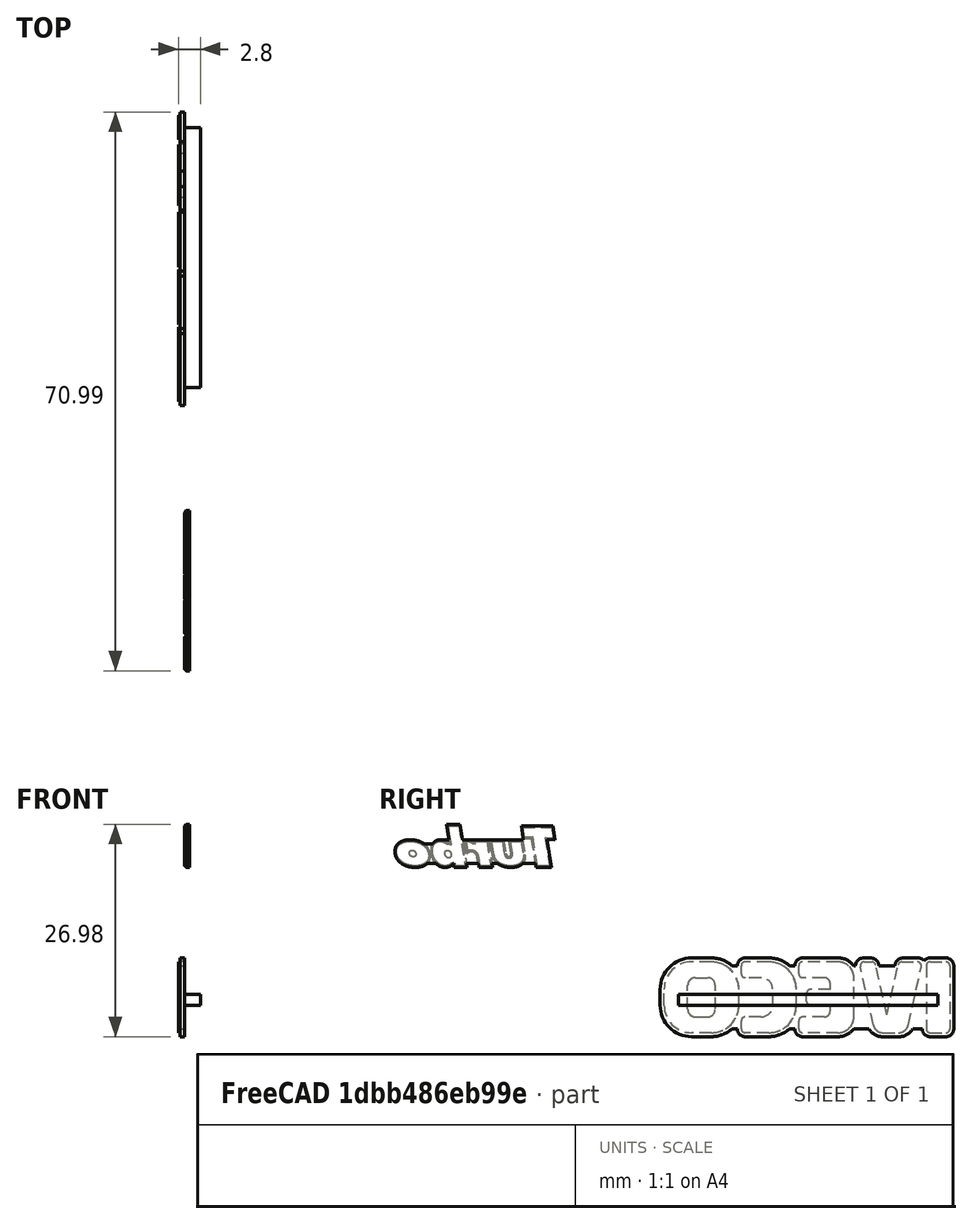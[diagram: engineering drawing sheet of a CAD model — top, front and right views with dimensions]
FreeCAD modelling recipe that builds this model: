
FCSTD DOCUMENT  (FreeCAD 0.16R6488 (Git))
Label: Iveco-logo
License: All rights reserved
LicenseURL: http://en.wikipedia.org/wiki/All_rights_reserved
objects: Part::Box×36, Part::Fillet×20, Part::MultiFuse×19, Part::Chamfer×16, Part::Part2DObjectPython×5, Part::Extrusion×5, Part::Cut×3, Part::Mirroring×2
note: 106 computed .brp shape members not serialized (recipe doc carries the construction recipe); baked Part::Feature solids carry a one-line shape summary decoded from their .brp

FEATURE [Part::Box] Box458  label="Cube683"
  Height = 9
  Length = 1
  Placement = pos=(-1,99,12) rot=(0,0,1;0rad)
  Width = 3
FEATURE [Part::Fillet] Fillet339
  Base = -> Box458
  Edges = 4 edges r=0.5: [Edge9,Edge10,Edge11,Edge12]
FEATURE [Part::Box] Box459  label="Cube684"
  Height = 10
  Length = 0.8
  Placement = pos=(-0.9,98.5,11.5) rot=(0,0,1;0rad)
  Width = 4
FEATURE [Part::Fillet] Fillet340
  Base = -> Box459
  Edges = 4 edges r=1: [Edge9,Edge10,Edge11,Edge12]
  Placement = pos=(0.1,0,0) rot=(0,0,1;0rad)
FEATURE [Part::Box] Box460  label="Cube685"
  Height = 2
  Length = 1
  Placement = pos=(-1,81.5,12) rot=(0,0,1;0rad)
  Width = 7
FEATURE [Part::Box] Box461  label="Cube686"
  Height = 3.5
  Length = 0.8
  Placement = pos=(-0.9,81,11.5) rot=(0,0,1;0rad)
  Width = 8
FEATURE [Part::Box] Box462  label="Cube687"
  Height = 2
  Length = 1
  Placement = pos=(-1,81.5,19) rot=(0,0,1;0rad)
  Width = 7
FEATURE [Part::Box] Box463  label="Cube688"
  Height = 3.5
  Length = 0.8
  Placement = pos=(-0.9,81,18) rot=(0,0,1;0rad)
  Width = 8
FEATURE [Part::Box] Box464  label="Cube689"
  Height = 9
  Length = 1
  Placement = pos=(-1,85.5,12) rot=(0,0,1;0rad)
  Width = 3
FEATURE [Part::Box] Box465  label="Cube690"
  Height = 10
  Length = 0.8
  Placement = pos=(-0.9,85,11.5) rot=(0,0,1;0rad)
  Width = 4
FEATURE [Part::Box] Box466  label="Cube691"
  Height = 2
  Length = 1
  Placement = pos=(-1,82.5,15.5) rot=(0,0,1;0rad)
  Width = 5
FEATURE [Part::Box] Box467  label="Cube692"
  Height = 3
  Length = 0.8
  Placement = pos=(-0.9,82.5,15) rot=(0,0,1;0rad)
  Width = 6
FEATURE [Part::MultiFuse] Fusion257
  Shapes = -> [Box460,Box466,Box462,Box464]
FEATURE [Part::Box] Box468  label="Cube693"
  Height = 2
  Length = 1
  Placement = pos=(-1,74.5,12) rot=(0,0,1;0rad)
  Width = 7
FEATURE [Part::Box] Box470  label="Cube695"
  Height = 2
  Length = 1
  Placement = pos=(-1,74.5,19) rot=(0,0,1;0rad)
  Width = 7
FEATURE [Part::Box] Box471  label="Cube696"
  Height = 9
  Length = 1
  Placement = pos=(-1,78.5,12) rot=(0,0,1;0rad)
  Width = 3
FEATURE [Part::Box] Box472  label="Cube697"
  Height = 3.5
  Length = 0.8
  Placement = pos=(-0.9,74,11.5) rot=(0,0,1;0rad)
  Width = 8
FEATURE [Part::Box] Box473  label="Cube698"
  Height = 3.5
  Length = 0.8
  Placement = pos=(-0.9,74,18) rot=(0,0,1;0rad)
  Width = 8
FEATURE [Part::Box] Box474  label="Cube699"
  Height = 10
  Length = 0.8
  Placement = pos=(-0.9,78,11.5) rot=(0,0,1;0rad)
  Width = 4
FEATURE [Part::MultiFuse] Fusion258
  Shapes = -> [Box468,Box470,Box471]
FEATURE [Part::MultiFuse] Fusion259
  Placement = pos=(0.1,0,0) rot=(0,0,1;0rad)
  Shapes = -> [Box472,Box473,Box474]
FEATURE [Part::MultiFuse] Fusion261  label="I"
  Placement = pos=(0,-1,0) rot=(0,0,1;0rad)
  Shapes = -> [Fillet339,Fillet340]
FEATURE [Part::Box] Box475  label="Cube700"
  Height = 2
  Length = 1
  Placement = pos=(-1,67.5,12) rot=(0,0,1;0rad)
  Width = 6
FEATURE [Part::Box] Box476  label="Cube701"
  Height = 2
  Length = 1
  Placement = pos=(-1,67.5,19) rot=(0,0,1;0rad)
  Width = 6
FEATURE [Part::Box] Box477  label="Cube702"
  Height = 9
  Length = 1
  Placement = pos=(-1,71.5,12) rot=(0,0,1;0rad)
  Width = 3
FEATURE [Part::Box] Box478  label="Cube703"
  Height = 3
  Length = 0.8
  Placement = pos=(-0.9,67,11) rot=(0,0,1;0rad)
  Width = 7
FEATURE [Part::Box] Box479  label="Cube704"
  Height = 3
  Length = 0.8
  Placement = pos=(-0.9,67,18) rot=(0,0,1;0rad)
  Width = 7
FEATURE [Part::Box] Box480  label="Cube705"
  Height = 10
  Length = 0.8
  Placement = pos=(-0.9,71,11) rot=(0,0,1;0rad)
  Width = 4
FEATURE [Part::Box] Box481  label="Cube706"
  Height = 9
  Length = 1
  Placement = pos=(-1,65,12) rot=(0,0,1;0rad)
  Width = 3
FEATURE [Part::Box] Box482  label="Cube707"
  Height = 10
  Length = 0.8
  Placement = pos=(-0.9,64.5,11) rot=(0,0,1;0rad)
  Width = 4
FEATURE [Part::MultiFuse] Fusion263
  Shapes = -> [Box475,Box476,Box477,Box481]
FEATURE [Part::MultiFuse] Fusion264
  Placement = pos=(0,0.5,0) rot=(0,0,1;0rad)
  Shapes = -> [Box478,Box479,Box480,Box482]
FEATURE [Part::Box] Box483  label="Cube708"
  Height = 9
  Length = 1
  Placement = pos=(-1,93,12) rot=(0,0,1;0rad)
  Width = 5
FEATURE [Part::Chamfer] Chamfer
  Base = -> Box483
  Edges = 1 edges: [Edge10 r1=8.99 r2=2]
FEATURE [Part::Chamfer] Chamfer001
  Base = -> Chamfer
  Edges = 1 edges: [Edge11 r1=2 r2=8.99]
FEATURE [Part::Box] Box485  label="Cube710"
  Height = 9
  Length = 1
  Placement = pos=(-1,93,12) rot=(0,0,1;0rad)
  Width = 4
FEATURE [Part::Chamfer] Chamfer002
  Base = -> Box485
  Edges = 1 edges: [Edge10 r1=8.99 r2=2]
FEATURE [Part::Chamfer] Chamfer003
  Base = -> Chamfer002
  Edges = 1 edges: [Edge11 r1=2 r2=8.99]
FEATURE [Part::Mirroring] Part__Mirroring  label="Chamfer003 (Mirror #1)"
  Base = (0,0,0)
  Normal = (0,1,0)
  Placement = pos=(0,187,0) rot=(0,0,1;0rad)
  Source = -> Chamfer003
FEATURE [Part::Box] Box486  label="Cube711"
  Height = 10
  Length = 0.8
  Placement = pos=(-1,93,12) rot=(0,0,1;0rad)
  Width = 6
FEATURE [Part::MultiFuse] Fusion266
  Shapes = -> [Chamfer001,Part__Mirroring]
FEATURE [Part::Box] Box488  label="Cube713"
  Height = 0.01
  Length = 1
  Placement = pos=(-1,89,20.99) rot=(0,0,1;0rad)
  Width = 10
FEATURE [Part::Cut] Cut
  Base = -> Fusion266
  Tool = -> Box488
FEATURE [Part::Fillet] Fillet356
  Base = -> Cut
  Edges = 4 edges r=0.5: [Edge8,Edge11,Edge17,Edge19]
FEATURE [Part::Fillet] Fillet357
  Base = -> Fillet356
  Edges = 2 edges r=1.25: [Edge27,Edge32]
FEATURE [Part::Box] Box489  label="Cube714"
  Height = 0.01
  Length = 1
  Placement = pos=(-1,89,21.49) rot=(0,0,1;0rad)
  Width = 10
FEATURE [Part::Box] Box490  label="Cube715"
  Height = 8
  Length = 0.8
  Placement = pos=(-0.8,68,12.5) rot=(0,0,1;0rad)
  Width = 30
FEATURE [Part::MultiFuse] Fusion
  Shapes = -> [Box461,Box465,Box467,Box463]
FEATURE [Part::Fillet] Fillet365
  Base = -> Fusion
  Edges = 2 edges r=1: [Edge3,Edge14]
FEATURE [Part::Fillet] Fillet366
  Base = -> Fillet365
  Edges = 2 edges r=2.5: [Edge25,Edge27]
  Placement = pos=(0.1,0,0) rot=(0,0,1;0rad)
FEATURE [Part::Chamfer] Chamfer008
  Base = -> Box486
  Edges = 1 edges: [Edge10 r1=9.99 r2=2]
FEATURE [Part::Chamfer] Chamfer009
  Base = -> Chamfer008
  Edges = 1 edges: [Edge11 r1=2 r2=9.99]
  Placement = pos=(0,-0.3,-0.5) rot=(0,0,1;0rad)
FEATURE [Part::Box] Box491  label="Cube716"
  Height = 10
  Length = 0.8
  Placement = pos=(-1,93,12) rot=(0,0,1;0rad)
  Width = 5
FEATURE [Part::Chamfer] Chamfer010
  Base = -> Box491
  Edges = 1 edges: [Edge10 r1=9.99 r2=2]
FEATURE [Part::Chamfer] Chamfer011
  Base = -> Chamfer010
  Edges = 1 edges: [Edge11 r1=2 r2=9.99]
FEATURE [Part::Mirroring] Part__Mirroring001  label="Chamfer011 (Mirror #2)"
  Base = (0,0,0)
  Normal = (0,1,0)
  Placement = pos=(0,187.3,-0.5) rot=(0,0,1;0rad)
  Source = -> Chamfer011
FEATURE [Part::MultiFuse] Fusion272
  Shapes = -> [Part__Mirroring001,Chamfer009]
FEATURE [Part::Cut] Cut001
  Base = -> Fusion272
  Placement = pos=(0.1,0,0) rot=(0,0,1;0rad)
  Tool = -> Box489
FEATURE [Part::Fillet] Fillet367
  Base = -> Cut001
  Edges = 4 edges r=1: [Edge8,Edge11,Edge17,Edge19]
FEATURE [Part::Fillet] Fillet368
  Base = -> Fillet367
  Edges = 2 edges r=2: [Edge27,Edge32]
  Placement = pos=(0.1,0,0) rot=(0,0,1;0rad)
FEATURE [Part::MultiFuse] Fusion273  label="V"
  Placement = pos=(0,-0.5,0) rot=(0,0,1;0rad)
  Shapes = -> [Fillet357,Fillet368]
FEATURE [Part::Fillet] Fillet369
  Base = -> Fusion259
  Edges = 2 edges r=4: [Edge20,Edge24]
FEATURE [Part::Fillet] Fillet370
  Base = -> Fillet369
  Edges = 4 edges r=1: [Edge13,Edge16,Edge26,Edge29]
FEATURE [Part::Fillet] Fillet371
  Base = -> Fillet370
  Edges = 2 edges r=0.3: [Edge31,Edge34]
FEATURE [Part::Box] Box495  label="Cube720"
  Height = 1.4
  Length = 2
  Placement = pos=(0,67,14.5) rot=(0,0,1;0rad)
  Width = 33
FEATURE [Part::Fillet] Fillet403
  Base = -> Fusion263
  Edges = 4 edges r=3.5: [Edge1,Edge3,Edge7,Edge9]
FEATURE [Part::Fillet] Fillet404
  Base = -> Fillet403
  Edges = 4 edges r=1: [Edge33,Edge34,Edge35,Edge36]
FEATURE [Part::Fillet] Fillet405
  Base = -> Fusion264
  Edges = 4 edges r=4: [Edge1,Edge3,Edge7,Edge9]
  Placement = pos=(0.1,-0.5,0.5) rot=(0,0,1;0rad)
FEATURE [Part::Fillet] Fillet406
  Base = -> Fusion258
  Edges = 4 edges r=0.5: [Edge1,Edge3,Edge13,Edge14]
FEATURE [Part::Fillet] Fillet407
  Base = -> Fillet406
  Edges = 2 edges r=3.5: [Edge30,Edge32]
FEATURE [Part::Fillet] Fillet408
  Base = -> Fillet407
  Edges = 2 edges r=1.5: [Edge33,Edge37]
FEATURE [Part::MultiFuse] Fusion295  label="C"
  Shapes = -> [Fillet371,Fillet408]
FEATURE [Part::MultiFuse] Fusion296  label="O"
  Placement = pos=(0,-0.3,0) rot=(0,0,1;0rad)
  Shapes = -> [Fillet405,Fillet404]
FEATURE [Part::Fillet] Fillet
  Base = -> Fusion257
  Edges = 6 edges r=0.5: [Edge1,Edge3,Edge19,Edge22,Edge23,Edge27]
FEATURE [Part::Fillet] Fillet409
  Base = -> Fillet
  Edges = 2 edges r=2: [Edge50,Edge52]
FEATURE [Part::Fillet] Fillet410
  Base = -> Fillet409
  Edges = 2 edges r=0.75: [Edge39,Edge53]
FEATURE [Part::MultiFuse] Fusion297  label="E"
  Placement = pos=(0,0.3,0) rot=(0,0,1;0rad)
  Shapes = -> [Fillet366,Fillet410]
FEATURE [Part::MultiFuse] Fusion298
  Placement = pos=(0,0.5,-1) rot=(0,0,1;0rad)
  Shapes = -> [Fusion273,Fusion261,Box490,Fusion297,Fusion295,Fusion296]
FEATURE [Part::Box] Box531  label="Cube756"
  Height = 10
  Length = 0.2
  Placement = pos=(-0.2,64,10.5) rot=(0,0,1;0rad)
  Width = 39
FEATURE [Part::Cut] Cut005
  Base = -> Fusion298
  Placement = pos=(0.2,0,0) rot=(0,0,1;0rad)
  Tool = -> Box531
FEATURE [Part::MultiFuse] Fusion299  label="iveco-logo_01"
  Shapes = -> [Box495,Cut005]
FEATURE [Part::Box] Box533  label="Cube758"
  Height = 2.5
  Length = 0.3
  Placement = pos=(0.3,32.5,32.5) rot=(0,0,1;0rad)
  Width = 17
FEATURE [Part::Part2DObjectPython] ShapeString003  # Draft 2D object (typed FeaturePython)
  FontFile = <path>
  Placement = pos=(0,52,32) rot=(0.57735,-0.57735,-0.57735;2.0944rad)
  Size = 1.35
  String = T
  Tracking = 0
FEATURE [Part::Part2DObjectPython] ShapeString004  # Draft 2D object (typed FeaturePython)
  FontFile = <path>
  Placement = pos=(0,48,32) rot=(0.57735,-0.57735,-0.57735;2.0944rad)
  Size = 1.3
  String = u
  Tracking = 0
FEATURE [Part::Part2DObjectPython] ShapeString005  # Draft 2D object (typed FeaturePython)
  FontFile = <path>
  Placement = pos=(0,43.75,32) rot=(0.57735,-0.57735,-0.57735;2.0944rad)
  Size = 1.3
  String = r
  Tracking = 0
FEATURE [Part::Part2DObjectPython] ShapeString006  # Draft 2D object (typed FeaturePython)
  FontFile = <path>
  Placement = pos=(0,40.5,32) rot=(0.57735,-0.57735,-0.57735;2.0944rad)
  Size = 1.3
  String = b
  Tracking = 0
FEATURE [Part::Part2DObjectPython] ShapeString007  # Draft 2D object (typed FeaturePython)
  FontFile = <path>
  Placement = pos=(0,36,32) rot=(0.57735,-0.57735,-0.57735;2.0944rad)
  Size = 1.3
  String = o
  Tracking = 0
FEATURE [Part::Extrusion] Extrude003
  Base = -> ShapeString007
  Dir = (0.6,0,0)
  Solid = false
FEATURE [Part::Extrusion] Extrude004
  Base = -> ShapeString006
  Dir = (0.6,0,0)
  Solid = false
FEATURE [Part::Extrusion] Extrude005
  Base = -> ShapeString005
  Dir = (0.6,0,0)
  Solid = false
FEATURE [Part::Extrusion] Extrude006
  Base = -> ShapeString004
  Dir = (0.6,0,0)
  Solid = false
FEATURE [Part::Extrusion] Extrude
  Base = -> ShapeString003
  Dir = (0.6,0,0)
  Solid = false
FEATURE [Part::Chamfer] Chamfer012
  Base = -> Extrude
  Edges = 8 edges r=0.2: [Edge3,Edge6,Edge9,Edge12,Edge15,Edge18,Edge21,Edge23]
FEATURE [Part::Chamfer] Chamfer013
  Base = -> Extrude006
  Edges = 6 edges r=0.2: [Edge3,Edge33,Edge36,Edge39,Edge57,Edge59]
FEATURE [Part::Chamfer] Chamfer014
  Base = -> Extrude005
  Edges = 3 edges r=0.2: [Edge15,Edge18,Edge21]
FEATURE [Part::Chamfer] Chamfer015
  Base = -> Chamfer014
  Edges = 1 edges r=0.2: [Edge28]
FEATURE [Part::Chamfer] Chamfer016
  Base = -> Chamfer015
  Edges = 1 edges r=0.2: [Edge12]
FEATURE [Part::Chamfer] Chamfer017
  Base = -> Chamfer016
  Edges = 1 edges r=0.2: [Edge4]
FEATURE [Part::Chamfer] Chamfer018
  Base = -> Extrude004
  Edges = 6 edges r=0.2: [Edge3,Edge6,Edge42,Edge57,Edge60,Edge62]
FEATURE [Part::Chamfer] Chamfer019
  Base = -> Extrude003
  Edges = 1 edges r=0.2: [Edge3]
FEATURE [Part::Box] Box534  label="Cube759"
  Height = 2
  Length = 0.3
  Placement = pos=(0.3,37,33.5) rot=(0,0,1;0rad)
  Width = 13
FEATURE [Part::Box] Box535  label="Cube760"
  Height = 2
  Length = 0.3
  Placement = pos=(0.3,47.3,34.5) rot=(0,0,1;0rad)
  Width = 2
FEATURE [Part::MultiFuse] Fusion301
  Shapes = -> [Chamfer012,Chamfer019,Chamfer013,Chamfer018,Chamfer017]
FEATURE [Part::MultiFuse] Fusion302
  Shapes = -> [Box533,Fusion301]
FEATURE [Part::MultiFuse] Fusion303
  Shapes = -> [Fusion302,Box535]
FEATURE [Part::MultiFuse] Fusion304  label="turbo-logo-01"
  Shapes = -> [Fusion303,Box534]
note: 5 file-system paths scrubbed to <path> (originals preserved in the JSON sidecar)
